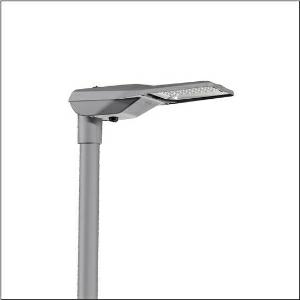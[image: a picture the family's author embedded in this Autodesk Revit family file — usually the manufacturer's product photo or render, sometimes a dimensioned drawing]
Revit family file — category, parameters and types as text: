
# Revit family: streetlight_sl_21_iq_mini___p0_8ab_5xe2r31y08gb_b9a0
name_source: partatom
category: Lighting Fixtures
units: mm (PartAtom-declared; Revit-internal decimal feet)

## family parameters
Cut with Voids When Loaded = No
Host = Face
Light Source = No
Part Type = Normal
Room Calculation Point = No
Round Connector Dimension = Use Diameter
Shared = No

## types (1)
- --- (1 x LED, 5200 lm, 39.8 W, 3000K)
    Apparent Load = 40 VA
    CIE Flux Codes = 36 71 98 100 100
    Color Rendering = 70
    Color Temperature = 3000K
    Default Elevation = 1800 mm
    Description = Streetlight SL 21 iQ mini, mast luminaire, primary light control with lens, of PMMA, primary optical cover: cover, of toughened safety glass, transparent, light distribution: P0.8aB, light emission: direct distribution, primary light characteristic: asymmetric, installation type: post-top, side-entry, LED, High Power LED, rated luminous flux: 5.200lm, luminous efficacy: 131lm/W, light colour: 730, colour temperature: 3000K, control gear: iQ-Street Remote, D4i with power reduction, control: pre-setting: logarithmic dimming characteristic, Street-Remote, Auto-Match, Temp-Guard, Lumen-Switch, Night-Set, Smart-Wire, Light-Fading, Desk-Remote (wireless, voltage-free reading and setting of iQ features in the workshop via application-optimized NFC function/RFID function), optimised constant luminous flux control (CLO 2.0), mains connection: 220..240V, AC, 50/60Hz, start of lifetime: 40W, end of service life: 41W, reduction: 18W, luminaire housing, of diecast aluminium, powder-coated, SITECO metallic grey (DB 702S), corrosivity category C5 high according to DIN EN ISO 12944, please order mast flange separately, inclination adjustable: 0°, 5°, 10°, 15°, sealing non-destructively replaceable, multi-level sealing system, length: 628mm, width: 235mm, height: 110mm, mast flange for spigot size: 42mm (side-entry): 5XC10008XM4, 60/48mm (side-entry/post-top): 5XC10108XM2, 76/60mm (side-entry/post-top): 5XC10108XM1, mounting height: 4..8m, Smart Interface below and above, protection rating (complete): IP66, insulation class (complete): insulation class II (safety insulation), certification: CE, ENEC, ENEC+, VDE, impact resistance: IK10, permissible operating ambient temperature for outdoor applications: -40..+50°C, standard-compliant lighting for roads and squares, packaging unit: 1 piece

Light Distribution: P0.8aB
    Height = 110 mm
    Lamp = 1 x LED
    Lamp Light Flux = 5200 lm
    Lamp Power = 39.8 W
    Lamp count = 1
    Length = 625 mm
    Luminous efficacy = 131 lm/W
    Manufacturer = Siteco
    ModVariant = No
    Model = 5XE2R31Y08GB
    Number of Poles = 1
    OnlyDefault = Yes
    Power Factor = 1
    Product Name = Streetlight SL 21 iQ mini | P0.8aB
    Product group = mast luminaire | pylon top
    ProductGroupID = 6100
    Protection Class = Protection class II
    Protection Degree = IP 66
    RLX_Detail_Level = 1
    RLX_Emergency_Light_Flux = 0 lm
    RLX_Emergency_Type = 0
    RLX_Emergency_Type_DB = No
    RlxData = <blob elided: 92481 chars, md5=c1af96fc>
    Socket = socket
    Standby Power = 0 W
    System Light Flux = 5200 lm
    System Power = 40 W
    Type Comments = factory setting: luminous flux: 100 % | dim-lin: 254 | 800 mA
    Type Image = l_1003514.jpg
    URL = http://relux.com
    VarID = @adj_083089
    Voltage = 0 V
    Weight = 0.00 kg
    Width = 234 mm

## geometry (parser evidence)
native form markers: Blend x4, Sweep x10
no freeform markers — native parametric forms only
